# Revit family: Plumbing-Fixtures_Accessibility-Professionals-Inc_62.625x38.25-Freedom-ADA-Roll-In-Shower-Center-Drain
name_source: partatom
category: Plumbing Fixtures
units: mm (PartAtom-declared; Revit-internal decimal feet)

## family parameters
Always vertical = Yes
Cut with Voids When Loaded = No
Enable Cutting in Views = No
Maintain Annotation Orientation = No
OmniClass Number = 23.45.05.14.11.21
OmniClass Title = Shower Receptors
Part Type = Normal
Room Calculation Point = No
Round Connector Dimension = Use Diameter
Shared = No
Work Plane-Based = No

## types (1)
- 62 ⅝" x 38 ¼" Freedom ADA Roll In Shower, CENTER drain
    Assembly Code = D2010.60
    Default Elevation = 0"
    Depth = 38 1/2"
    Description = Five-piece ADA roll-in shower stall for remodels. Inside dimensions 60″ x 36″ for ADA compliance, 3/4″ beveled threshold, center drain, pre-leveled base, full wood-backing, subway-tile look with durable applied-acrylic finish. 30-year warranty, made in the USA. Order with a folding shower seat, grab bars, and accessories to meet ADAAG guidelines.
    Drain Diameter = 2"
    Flow = 0 GPM
    Grab Bars Material = Freedom Showers by Accessibility Professionals Inc. - Steel - Stainless
    Height = 79"
    Horizontal Drain Offset = 19 1/2"
    Interior Depth = 36"
    Interior Width = 60"
    Internal Wall Offset Back = 1"
    Internal Wall Offset Side = 1"
    Keynote = 22 40 00.B5
    Manufacturer = Freedom Showers by Accessibility Professionals Inc.
    Model = APF6238BF5P.75
    Product Documentation Link = https://www.freedomshowers.com
    Product Material = Freedom Showers by Accessibility Professionals Inc. - Fiberglass Acrylic - White
    Product Page URL = https://www.freedomshowers.com
    Threshold Height = 1"
    URL = https://www.freedomshowers.com
    Version = 1
    Vertical Drain Offset = 31 1/2"
    Water Inlet Diameter = 2"
    Width = 62 1/2"

## geometry (parser evidence)
native form markers: Sweep x1
no freeform markers — native parametric forms only
